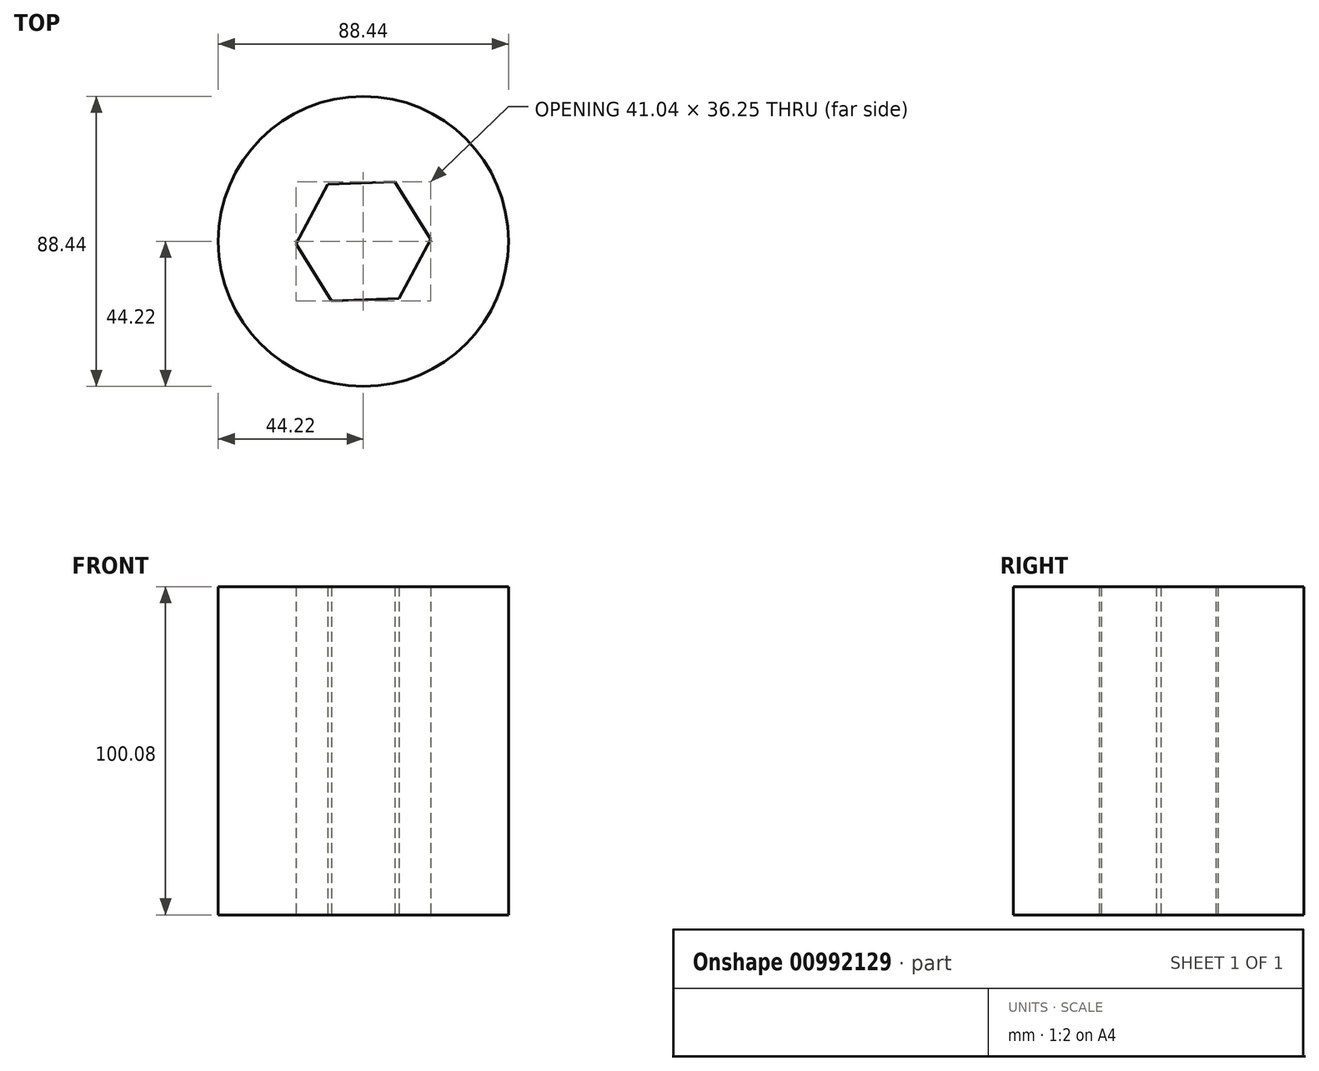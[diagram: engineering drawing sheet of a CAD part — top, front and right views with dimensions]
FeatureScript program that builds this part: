
annotation { "Feature Type Name" : "Feature", "Feature Type Description" : "" }
export const myFeature = defineFeature(function(context is Context, id is Id, definition is map)
    precondition{}
    {
        {
            var Q0;
            Q0=qCreatedBy(makeId("Top.planeOp"),FACE);
            var sketch = newSketch(context, id + "F0", { "sketchPlane" : qUnion([Q0])});
            skCircle(sketch, "E0", {"center": v(0, 0) * mm, "radius": 44.22 * mm});
            skCircle(sketch, "E1.cCircle", {"center": v(0, 0) * mm, "radius": 17.78 * mm, "construction": true});
            skLineSegment(sketch, "E1.0", {"start": v(-20.52, -0.7) * mm, "end": v(-10.87, 17.42) * mm});
            skLineSegment(sketch, "E1.1", {"start": v(-10.87, 17.42) * mm, "end": v(9.65, 18.12) * mm});
            skLineSegment(sketch, "E1.2", {"start": v(9.65, 18.12) * mm, "end": v(20.52, 0.7) * mm});
            skLineSegment(sketch, "E1.3", {"start": v(20.52, 0.7) * mm, "end": v(10.87, -17.42) * mm});
            skLineSegment(sketch, "E1.4", {"start": v(10.87, -17.42) * mm, "end": v(-9.65, -18.12) * mm});
            skLineSegment(sketch, "E1.5", {"start": v(-9.65, -18.12) * mm, "end": v(-20.52, -0.7) * mm});
            skPoint(sketch, "E1.0.midPoint", {"position": v(-15.7, 8.36) * mm});
            skSolve(sketch);
        }
        {
            var Q0;
            Q0=makeQuery(id+"F0.imprint","IMPRINT",FACE,{"disambiguationData":[TD([[makeQuery(id+"F0.imprint","IMPRINT",EDGE,{"derivedFrom":sQuery(id+"F0.wireOp",EDGE,"E0")}),1.0]])]});
            extrude(context, id + "F1", {"entities" : qUnion([Q0]), "depth" : 100.08 * mm, "offsetDistance" : 25.4 * mm});
        }
    });
